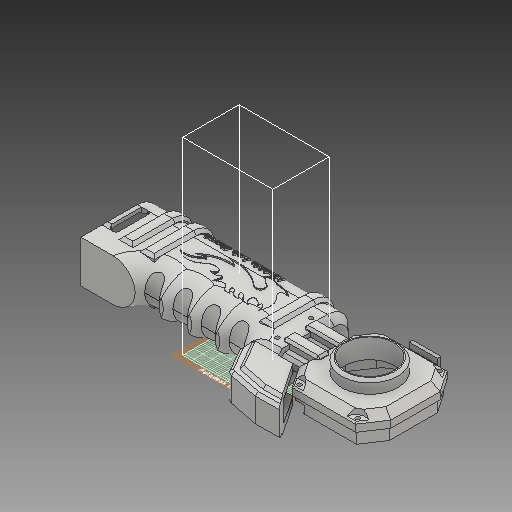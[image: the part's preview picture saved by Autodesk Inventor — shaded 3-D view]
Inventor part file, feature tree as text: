
AUTODESK INVENTOR PART (.ipt)
format: ipt  version: 2018 (Build 220112000, 112)  size: 7,969,280 bytes
history: native  units: mm
features: extrude x9, sketch x9, chamfer x7, other x6, mirror x4, fillet x1, projected_geometry x1
ambient origin geometry x8: Origin, YZ Plane, XZ Plane, XY Plane, X Axis, Y Axis, Z Axis, Center Point
bodies: Body1 (feature_tree)
feature tree (37):
  other  "underassy.iam"
  other  "undercover.ipt:1"
  other  "dragon.ipt:1"
  other  "dragon_MIR.ipt:1"
  other  "ソリッド1"
  extrude  "押し出し1"  Depth=10.0mm
  extrude  "押し出し2"  Depth=10.0mm TaperAngle=0.0deg
  chamfer  "面取り1"  Distance=25.0mm
  other  "作業平面1"
  mirror  "ミラー1"
  extrude  "押し出し4"  Depth=10.0mm
  extrude  "押し出し5"  Depth=15.0mm
  mirror  "ミラー2"
  chamfer  "面取り2"  Distance=2.0mm
  fillet  "フィレット1"  Radius=2.0mm
  chamfer  "面取り4"  [1 undecoded]
  extrude  "押し出し6"  Depth=2.0mm TaperAngle=0.0deg
  chamfer  "面取り5"  Distance=1.5mm
  extrude  "押し出し7"  Depth=2.0mm TaperAngle=0.0deg
  extrude  "押し出し8"  Depth=1.5mm TaperAngle=45.0deg
  mirror  "ミラー3"
  chamfer  "面取り6"  Distance=2.0mm
  chamfer  "面取り7"  Distance=1.0mm Angle=45.0deg
  extrude  "押し出し9"  Depth=5.0mm TaperAngle=0.0deg
  extrude  "押し出し10"  Depth=2.0mm TaperAngle=45.0deg
  mirror  "ミラー4"
  chamfer  "面取り8"  Distance=3.0mm
  sketch  "スケッチ1"
  projected_geometry  "投影ループ1"
  sketch  "スケッチ2"
  sketch  "スケッチ4"
  sketch  "スケッチ5"
  sketch  "スケッチ6"
  sketch  "スケッチ7"
  sketch  "スケッチ8"
  sketch  "スケッチ9"
  sketch  "スケッチ10"
note: 1 required parameter value undecoded (feature->parameter linkage not recoverable at this tier; creation-order binding heuristic only, values carry confidence <= 0.55)
